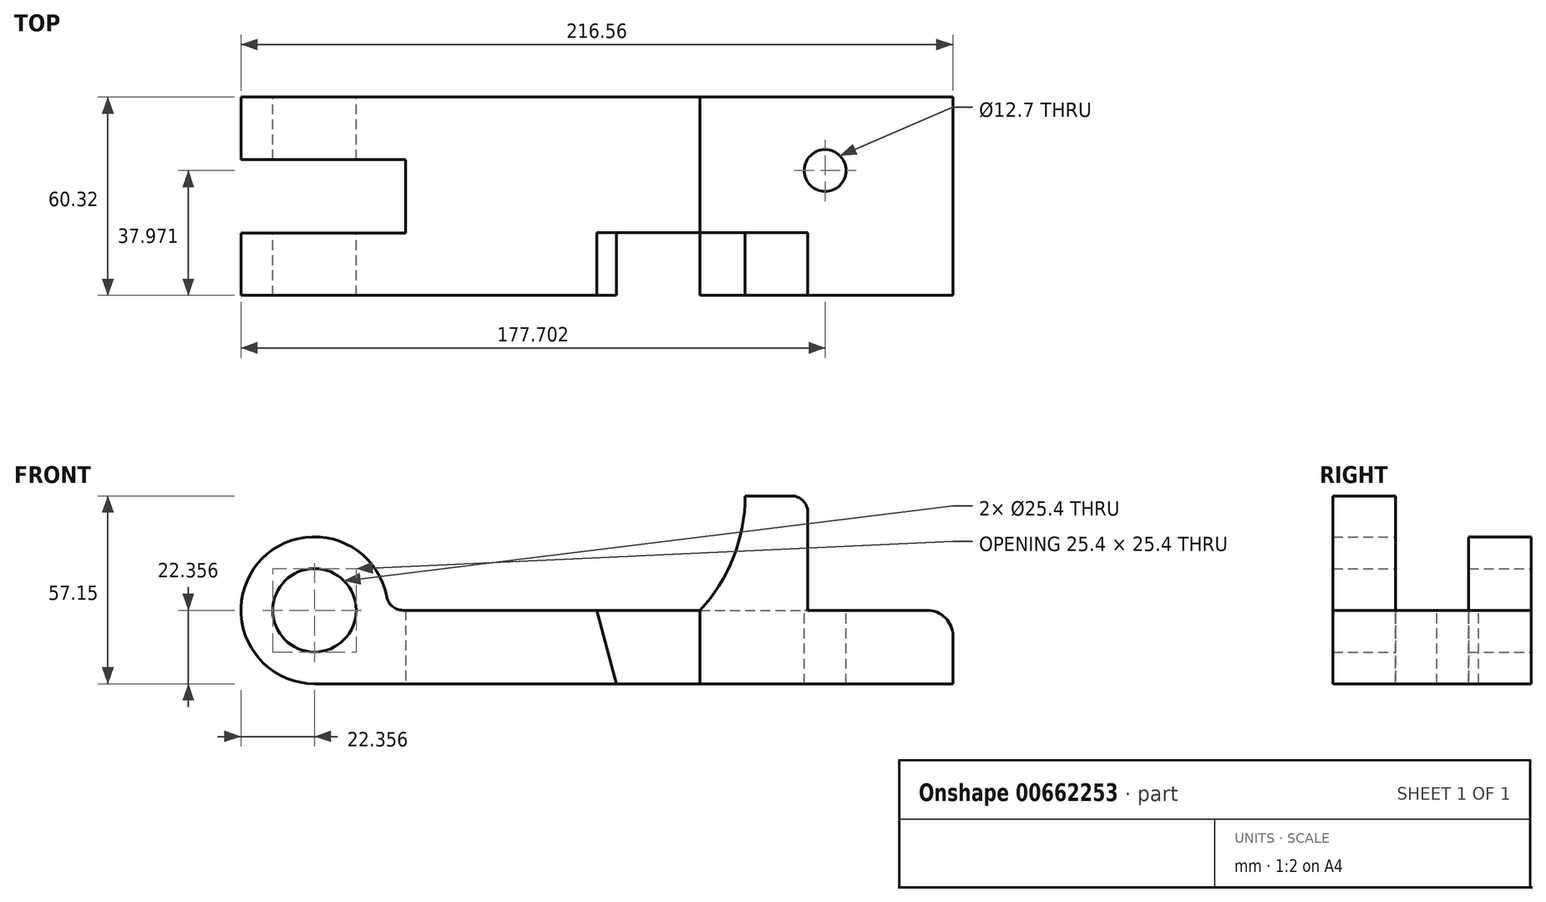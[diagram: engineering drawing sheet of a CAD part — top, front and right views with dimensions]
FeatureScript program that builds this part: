
annotation { "Feature Type Name" : "Feature", "Feature Type Description" : "" }
export const myFeature = defineFeature(function(context is Context, id is Id, definition is map)
    precondition{}
    {
        {
            var Q0;
            Q0=qCreatedBy(makeId("Front.planeOp"),FACE);
            var sketch = newSketch(context, id + "F0", { "sketchPlane" : qUnion([Q0])});
            skLineSegment(sketch, "E0.bottom", {"start": v(-97.1, 11.18) * mm, "end": v(97.1, 11.18) * mm});
            skLineSegment(sketch, "E0.top", {"start": v(-97.1, -11.18) * mm, "end": v(97.1, -11.18) * mm});
            skLineSegment(sketch, "E0.left", {"start": v(-97.1, 11.18) * mm, "end": v(-97.1, -11.18) * mm});
            skLineSegment(sketch, "E0.right", {"start": v(97.1, 11.18) * mm, "end": v(97.1, -11.18) * mm});
            skPoint(sketch, "E0.middle", {"position": v(0, 0) * mm});
            skCircle(sketch, "E1", {"center": v(-97.1, 11.18) * mm, "radius": 22.35 * mm});
            skCircle(sketch, "E2", {"center": v(-97.1, 11.18) * mm, "radius": 12.7 * mm});
            skLineSegment(sketch, "E3", {"start": v(-11.25, 11.18) * mm, "end": v(-5.26, -11.18) * mm});
            skLineSegment(sketch, "E4", {"start": v(33.93, 11.18) * mm, "end": v(33.93, 45.97) * mm});
            skLineSegment(sketch, "E5", {"start": v(33.93, 45.97) * mm, "end": v(52.98, 45.97) * mm});
            skLineSegment(sketch, "E6", {"start": v(52.98, 45.97) * mm, "end": v(52.98, 11.18) * mm});
            skArc(sketch, "E7", {"start": v(20.14, 11.17) * mm, "mid": v(30.36, 27.26) * mm, "end": v(33.93, 45.97) * mm});
            skLineSegment(sketch, "E8", {"start": v(20.14, 11.18) * mm, "end": v(20.14, -11.18) * mm});
            skSolve(sketch);
        }
        {
            var Q0;
            {var subQ0=sQuery(id+"F0.wireOp",EDGE,"E1");var subQ1=sQuery(id+"F0.wireOp",EDGE,"E0.bottom");var subQ2=makeQuery(id+"F0.imprint","INTERSECT",VERTEX,{"derivedFrom":[subQ1,subQ0]});Q0=makeQuery(id+"F0.imprint","IMPRINT",FACE,{"disambiguationData":[TD([[makeQuery(id+"F0.imprint","IMPRINT",EDGE,{"disambiguationData":[TD([[subQ2,1.0]])],"derivedFrom":subQ1}),1.0]])]});}
            var Q1;
            {var subQ0=sQuery(id+"F0.wireOp",EDGE,"E1");var subQ1=sQuery(id+"F0.wireOp",EDGE,"E0.bottom");var subQ2=makeQuery(id+"F0.imprint","INTERSECT",VERTEX,{"derivedFrom":[subQ1,subQ0]});Q1=makeQuery(id+"F0.imprint","IMPRINT",FACE,{"disambiguationData":[TD([[makeQuery(id+"F0.imprint","IMPRINT",EDGE,{"disambiguationData":[TD([[subQ2,1.0]])],"derivedFrom":subQ1}),-1.0]])]});}
            var Q2;
            {var subQ0=sQuery(id+"F0.wireOp",EDGE,"E3");Q2=makeQuery(id+"F0.imprint","IMPRINT",FACE,{"disambiguationData":[TD([[makeQuery(id+"F0.imprint","IMPRINT",EDGE,{"derivedFrom":subQ0}),-1.0]])]});}
            var Q3;
            {var subQ0=sQuery(id+"F0.wireOp",EDGE,"E3");Q3=makeQuery(id+"F0.imprint","IMPRINT",FACE,{"disambiguationData":[TD([[makeQuery(id+"F0.imprint","IMPRINT",EDGE,{"derivedFrom":subQ0}),1.0]])]});}
            var Q4;
            {var subQ0=sQuery(id+"F0.wireOp",EDGE,"E0.right");Q4=makeQuery(id+"F0.imprint","IMPRINT",FACE,{"disambiguationData":[TD([[makeQuery(id+"F0.imprint","IMPRINT",EDGE,{"derivedFrom":subQ0}),-1.0]])]});}
            extrude(context, id + "F1", {"entities" : qUnion([Q0, Q1, Q2, Q3, Q4]), "endBound" : BoundingType.SYMMETRIC, "depth" : 60.32 * mm, "offsetDistance" : 25.4 * mm});
        }
        {
            var Q0;
            {var subQ0=sQuery(id+"F0.wireOp",EDGE,"E4");Q0=makeQuery(id+"F0.imprint","IMPRINT",FACE,{"disambiguationData":[TD([[makeQuery(id+"F0.imprint","IMPRINT",EDGE,{"derivedFrom":subQ0}),-1.0]])]});}
            var Q1;
            {var subQ0=sQuery(id+"F0.wireOp",EDGE,"E4");Q1=makeQuery(id+"F0.imprint","IMPRINT",FACE,{"disambiguationData":[TD([[makeQuery(id+"F0.imprint","IMPRINT",EDGE,{"derivedFrom":subQ0}),1.0]])]});}
            extrude(context, id + "F2", {"entities" : qUnion([Q0, Q1]), "operationType" : NewBodyOperationType.ADD, "depth" : 30.16 * mm, "offsetDistance" : 25.4 * mm});
        }
        {
            var Q0;
            {var subQ0=sQuery(id+"F0.wireOp",EDGE,"E4");Q0=makeQuery(id+"F0.imprint","IMPRINT",FACE,{"disambiguationData":[TD([[makeQuery(id+"F0.imprint","IMPRINT",EDGE,{"derivedFrom":subQ0}),-1.0]])]});}
            var Q1;
            {var subQ0=sQuery(id+"F0.wireOp",EDGE,"E4");Q1=makeQuery(id+"F0.imprint","IMPRINT",FACE,{"disambiguationData":[TD([[makeQuery(id+"F0.imprint","IMPRINT",EDGE,{"derivedFrom":subQ0}),1.0]])]});}
            extrude(context, id + "F3", {"entities" : qUnion([Q0, Q1]), "operationType" : NewBodyOperationType.REMOVE, "depth" : 11.1 * mm, "offsetDistance" : 25.4 * mm});
        }
        {
            var Q0;
            {var subQ0=sQuery(id+"F0.wireOp",EDGE,"E0.bottom");Q0=makeQuery(id+"F3.boolean.opBoolean","MERGE",FACE,{"derivedFrom":[makeQuery(id+"F1.opExtrude","SWEPT_FACE",FACE,{"disambiguationData":[OSD([subQ0])]}),makeQuery(id+"F3.opExtrude","SWEPT_FACE",FACE,{"disambiguationData":[OSD([subQ0])]})]});}
            var sketch = newSketch(context, id + "F4", { "sketchPlane" : qUnion([Q0])});
            skCircle(sketch, "E9", {"center": v(58.24, 7.81) * mm, "radius": 6.35 * mm});
            skSolve(sketch);
        }
        {
            var Q0;
            Q0=makeQuery(id+"F4.imprint","IMPRINT",FACE,{"disambiguationData":[TD([[makeQuery(id+"F4.imprint","IMPRINT",EDGE,{"derivedFrom":sQuery(id+"F4.wireOp",EDGE,"E9")}),1.0]])]});
            extrude(context, id + "F5", {"entities" : qUnion([Q0]), "operationType" : NewBodyOperationType.REMOVE, "endBound" : BoundingType.THROUGH_ALL, "oppositeDirection" : true, "depth" : 25.4 * mm, "offsetDistance" : 25.4 * mm});
        }
        {
            var Q0;
            {var subQ0=sQuery(id+"F0.wireOp",EDGE,"E0.bottom");Q0=makeQuery(id+"F2.boolean.opBoolean","MERGE",FACE,{"derivedFrom":[makeQuery(id+"F1.opExtrude","CAP_FACE",FACE,{"disambiguationData":[OSD([subQ0,sQuery(id+"F0.wireOp",EDGE,"E0.top"),sQuery(id+"F0.wireOp",EDGE,"E0.right"),sQuery(id+"F0.wireOp",EDGE,"E1"),sQuery(id+"F0.wireOp",EDGE,"E2")])],"isStart":false}),makeQuery(id+"F2.opExtrude","CAP_FACE",FACE,{"disambiguationData":[OSD([subQ0,sQuery(id+"F0.wireOp",EDGE,"E5"),sQuery(id+"F0.wireOp",EDGE,"E6"),sQuery(id+"F0.wireOp",EDGE,"E7")])],"isStart":false})]});}
            var sketch = newSketch(context, id + "F6", { "sketchPlane" : qUnion([Q0])});
            skLineSegment(sketch, "E10.0", {"start": v(20.14, 11.17) * mm, "end": v(20.14, -11.18) * mm});
            skLineSegment(sketch, "E10.1", {"start": v(-11.25, 11.18) * mm, "end": v(-5.26, -11.18) * mm});
            skSolve(sketch);
        }
        {
            var Q0;
            {var subQ6=sQuery(id+"F6.wireOp",EDGE,"E10.0");Q0=makeQuery(id+"F6.imprint","IMPRINT",FACE,{"disambiguationData":[TD([[makeQuery(id+"F6.imprint","IMPRINT",EDGE,{"derivedFrom":subQ6}),-1.0]])]});}
            extrude(context, id + "F7", {"entities" : qUnion([Q0]), "operationType" : NewBodyOperationType.REMOVE, "oppositeDirection" : true, "depth" : 19.05 * mm, "offsetDistance" : 25.4 * mm});
        }
        {
            var Q0;
            Q0=qCreatedBy(makeId("Top.planeOp"),FACE);
            var sketch = newSketch(context, id + "F8", { "sketchPlane" : qUnion([Q0])});
            skLineSegment(sketch, "E11.bottom", {"start": v(-183.68, -11.16) * mm, "end": v(-69.38, -11.16) * mm});
            skLineSegment(sketch, "E11.top", {"start": v(-183.68, 11.16) * mm, "end": v(-69.38, 11.16) * mm});
            skLineSegment(sketch, "E11.left", {"start": v(-183.68, -11.16) * mm, "end": v(-183.68, 11.16) * mm});
            skLineSegment(sketch, "E11.right", {"start": v(-69.38, -11.16) * mm, "end": v(-69.38, 11.16) * mm});
            skPoint(sketch, "E11.middle", {"position": v(-126.53, 0) * mm});
            skSolve(sketch);
        }
        {
            var Q0;
            Q0=makeQuery(id+"F8.imprint","IMPRINT",FACE,{"disambiguationData":[TD([[makeQuery(id+"F8.imprint","IMPRINT",EDGE,{"derivedFrom":sQuery(id+"F8.wireOp",EDGE,"E11.bottom")}),1.0]])]});
            extrude(context, id + "F9", {"entities" : qUnion([Q0]), "operationType" : NewBodyOperationType.REMOVE, "endBound" : BoundingType.SYMMETRIC, "depth" : 177.8 * mm, "offsetDistance" : 25.4 * mm});
        }
        {
            var Q0;
            {var subQ0=sQuery(id+"F0.wireOp",EDGE,"E0.bottom");var subQ3=sQuery(id+"F0.wireOp",EDGE,"E1");Q0=makeQuery(id+"F9.boolean.opBoolean","SPLIT",EDGE,{"disambiguationData":[TD([makeQuery(id+"F9.opExtrude","SWEPT_FACE",FACE,{"disambiguationData":[OSD([sQuery(id+"F8.wireOp",EDGE,"E11.top")])]})])],"derivedFrom":makeQuery(id+"F1.opExtrude","SWEPT_EDGE",EDGE,{"disambiguationData":[OSD([subQ0,subQ3])]})});}
            var Q1;
            {var subQ1=sQuery(id+"F0.wireOp",EDGE,"E0.bottom");var subQ2=sQuery(id+"F0.wireOp",EDGE,"E1");Q1=makeQuery(id+"F9.boolean.opBoolean","SPLIT",EDGE,{"disambiguationData":[TD([makeQuery(id+"F9.opExtrude","SWEPT_FACE",FACE,{"disambiguationData":[OSD([sQuery(id+"F8.wireOp",EDGE,"E11.bottom")])]})])],"derivedFrom":makeQuery(id+"F1.opExtrude","SWEPT_EDGE",EDGE,{"disambiguationData":[OSD([subQ1,subQ2])]})});}
            var Q2;
            Q2=makeQuery(id+"F2.opExtrude","SWEPT_EDGE",EDGE,{"disambiguationData":[OSD([sQuery(id+"F0.wireOp",EDGE,"E0.bottom"),sQuery(id+"F0.wireOp",EDGE,"E6")])]});
            var Q3;
            Q3=makeQuery(id+"F2.opExtrude","SWEPT_EDGE",EDGE,{"disambiguationData":[OSD([sQuery(id+"F0.wireOp",EDGE,"E5"),sQuery(id+"F0.wireOp",EDGE,"E6")])]});
            fillet(context, id + "F10", {"entities" : qUnion([Q0, Q1, Q2, Q3]), "radius" : 5.08 * mm, "tangentPropagation" : true, "allowEdgeOverflow" : false});
        }
        {
            var Q0;
            Q0=makeQuery(id+"F1.opExtrude","SWEPT_EDGE",EDGE,{"disambiguationData":[OSD([sQuery(id+"F0.wireOp",EDGE,"E0.bottom"),sQuery(id+"F0.wireOp",EDGE,"E0.right")])]});
            fillet(context, id + "F11", {"entities" : qUnion([Q0]), "radius" : 7.87 * mm, "tangentPropagation" : true, "allowEdgeOverflow" : false});
        }
    });
